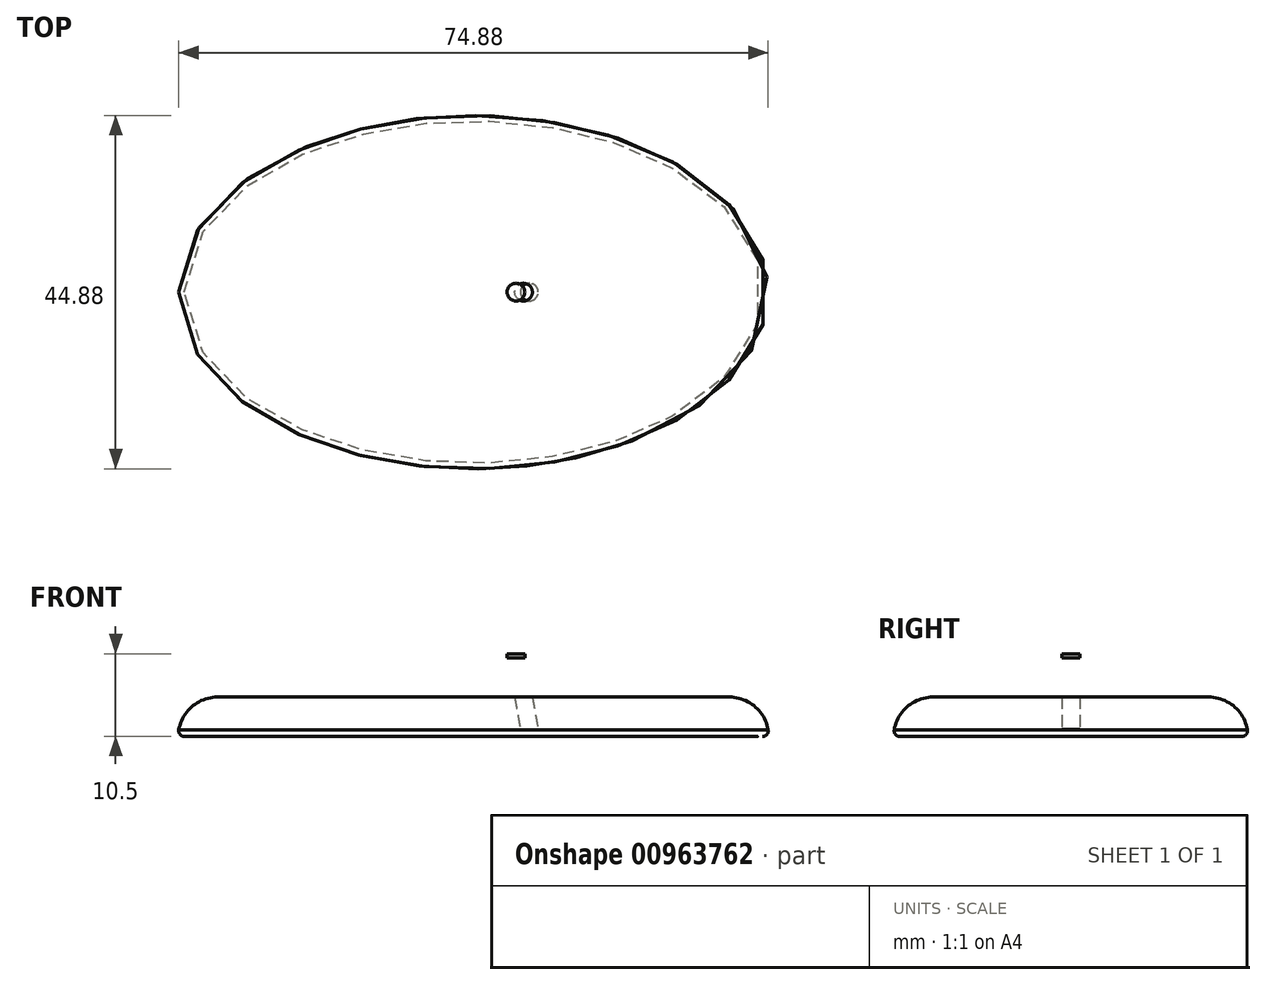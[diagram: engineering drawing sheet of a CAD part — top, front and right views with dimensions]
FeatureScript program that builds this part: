
annotation { "Feature Type Name" : "Feature", "Feature Type Description" : "" }
export const myFeature = defineFeature(function(context is Context, id is Id, definition is map)
    precondition{}
    {
        {
            var Q0;
            Q0=qCreatedBy(makeId("Top.planeOp"),FACE);
            var sketch = newSketch(context, id + "F0", { "sketchPlane" : qUnion([Q0])});
            skEllipse(sketch, "E0", {"center": v(0, 0) * mm, "majorRadius": 37.5 * mm, "minorRadius": 22.5 * mm, "majorAxis": v(-1, 0)});
            skSolve(sketch);
        }
        {
            var Q0;
            Q0 = qSketchRegion(id + "F0", true);
            extrude(context, id + "F1", {"entities" : qUnion([Q0]), "depth" : 5 * mm, "offsetDistance" : 25 * mm});
        }
        {
            var Q0;
            Q0=makeQuery(id+"F1.opExtrude","CAP_FACE",FACE,{"disambiguationData":[OSD([sQuery(id+"F0.wireOp",EDGE,"E0")])],"isStart":false});
            cPlane(context, id + "F2", {"entities" : qUnion([Q0]), "cplaneType" : CPlaneType.OFFSET, "offset" : 5 * mm, "width" : 150 * mm, "height" : 150 * mm});
        }
        {
            var Q0;
            Q0=qCreatedBy(id+"F2.planeOp",FACE);
            var sketch = newSketch(context, id + "F3", { "sketchPlane" : qUnion([Q0])});
            skCircle(sketch, "E1", {"center": v(5.4, 0) * mm, "radius": 1.13 * mm});
            skSolve(sketch);
        }
        {
            var Q0;
            Q0=qCreatedBy(makeId("Front.planeOp"),FACE);
            var sketch = newSketch(context, id + "F4", { "sketchPlane" : qUnion([Q0])});
            skLineSegment(sketch, "E2", {"start": v(7.68, 11.11) * mm, "end": v(9.48, 0.9) * mm});
            skSolve(sketch);
        }
        {
            var Q0;
            Q0=makeQuery(id+"F3.imprint","IMPRINT",FACE,{"disambiguationData":[TD([[makeQuery(id+"F3.imprint","IMPRINT",EDGE,{"derivedFrom":sQuery(id+"F3.wireOp",EDGE,"E1")}),1.0]])]});
            extrude(context, id + "F5", {"entities" : qUnion([Q0]), "depth" : .5 * mm, "offsetDistance" : 25 * mm});
        }
        {
            var Q0;
            Q0=makeQuery(id+"F5.opExtrude","CAP_FACE",FACE,{"disambiguationData":[OSD([sQuery(id+"F3.wireOp",EDGE,"E1")])],"isStart":false});
            var Q1;
            Q1=sQuery(id+"F4.wireOp",EDGE,"E2");
            sweep(context, id + "F6", {"profiles" : qUnion([Q0]), "path" : qUnion([Q1])});
        }
        {
            var Q0;
            Q0=makeQuery(id+"F6.opSweep","SWEPT_BODY",BODY,{"disambiguationData":[OSD([sQuery(id+"F3.wireOp",EDGE,"E1"),sQuery(id+"F4.wireOp",EDGE,"E2")])]});
            var Q1;
            Q1=makeQuery(id+"F1.opExtrude","SWEPT_BODY",BODY,{"disambiguationData":[OSD([sQuery(id+"F0.wireOp",EDGE,"E0")])]});
            booleanBodies(context, id + "F7", {"operationType" : BooleanOperationType.SUBTRACTION, "tools" : qUnion([Q0]), "targets" : qUnion([Q1])});
        }
        {
            var Q0;
            Q0=makeQuery(id+"F1.opExtrude","CAP_EDGE",EDGE,{"disambiguationData":[OSD([sQuery(id+"F0.wireOp",EDGE,"E0")])],"isStart":false});
            fillet(context, id + "F8", {"entities" : qUnion([Q0]), "radius" : 5 * mm, "tangentPropagation" : true, "allowEdgeOverflow" : false});
        }
        {
            var Q0;
            {var subQ0=sQuery(id+"F0.wireOp",EDGE,"E0");Q0=makeQuery(id+"F8.opFillet","BLEND_EDGE",EDGE,{"blendedFrom":[makeQuery(id+"F1.opExtrude","CAP_EDGE",EDGE,{"disambiguationData":[OSD([subQ0])],"isStart":false}),makeQuery(id+"F1.opExtrude","CAP_FACE",FACE,{"disambiguationData":[OSD([subQ0])],"isStart":true})],"blendedInto":[makeQuery(id+"F1.opExtrude","CAP_FACE",FACE,{"disambiguationData":[OSD([subQ0])],"isStart":true})]});}
            fillet(context, id + "F9", {"entities" : qUnion([Q0]), "radius" : 0.7 * mm, "tangentPropagation" : true, "allowEdgeOverflow" : false});
        }
    });
